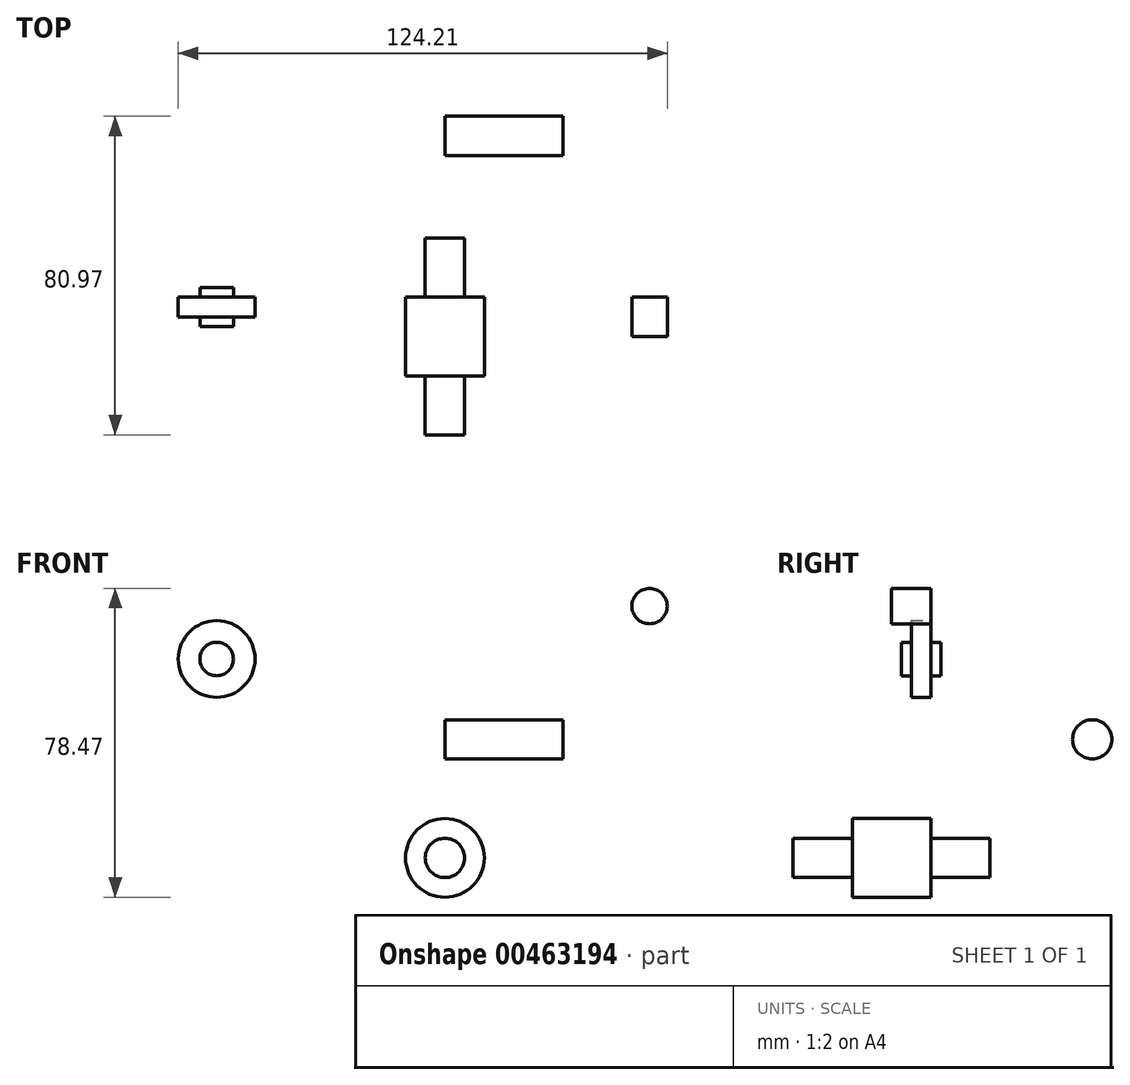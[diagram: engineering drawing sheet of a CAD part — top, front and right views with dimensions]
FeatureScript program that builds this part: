
annotation { "Feature Type Name" : "Feature", "Feature Type Description" : "" }
export const myFeature = defineFeature(function(context is Context, id is Id, definition is map)
    precondition{}
    {
        {
            var Q0;
            Q0=qCreatedBy(makeId("Front.planeOp"),FACE);
            var sketch = newSketch(context, id + "F0", { "sketchPlane" : qUnion([Q0])});
            skCircle(sketch, "E0", {"center": v(0, 0) * mm, "radius": 10 * mm});
            skCircle(sketch, "E1", {"center": v(0, 0) * mm, "radius": 4.99 * mm});
            skCircle(sketch, "E2", {"center": v(-57.98, 50.53) * mm, "radius": 9.75 * mm});
            skCircle(sketch, "E3", {"center": v(-57.98, 50.53) * mm, "radius": 4.25 * mm});
            skCircle(sketch, "E4", {"center": v(52, 63.98) * mm, "radius": 4.49 * mm});
            skSolve(sketch);
        }
        {
            var Q0;
            Q0=makeQuery(id+"F0.imprint","IMPRINT",FACE,{"disambiguationData":[TD([[makeQuery(id+"F0.imprint","IMPRINT",EDGE,{"derivedFrom":sQuery(id+"F0.wireOp",EDGE,"E0")}),1.0]])]});
            var Q1;
            Q1=makeQuery(id+"F0.imprint","IMPRINT",FACE,{"disambiguationData":[TD([[makeQuery(id+"F0.imprint","IMPRINT",EDGE,{"derivedFrom":sQuery(id+"F0.wireOp",EDGE,"E1")}),1.0]])]});
            extrude(context, id + "F1", {"entities" : qUnion([Q0, Q1]), "depth" : 20 * mm});
        }
        {
            var Q0;
            Q0=makeQuery(id+"F0.imprint","IMPRINT",FACE,{"disambiguationData":[TD([[makeQuery(id+"F0.imprint","IMPRINT",EDGE,{"derivedFrom":sQuery(id+"F0.wireOp",EDGE,"E1")}),1.0]])]});
            extrude(context, id + "F2", {"entities" : qUnion([Q0]), "operationType" : NewBodyOperationType.ADD, "oppositeDirection" : true, "depth" : 15 * mm});
        }
        {
            var Q0;
            Q0=makeQuery(id+"F1.opExtrude","CAP_FACE",FACE,{"disambiguationData":[OSD([sQuery(id+"F0.wireOp",EDGE,"E0")])],"isStart":false});
            var sketch = newSketch(context, id + "F3", { "sketchPlane" : qUnion([Q0])});
            skCircle(sketch, "E5.0", {"center": v(0, 0) * mm, "radius": 4.99 * mm});
            skSolve(sketch);
        }
        {
            var Q0;
            Q0=makeQuery(id+"F3.imprint","IMPRINT",FACE,{"disambiguationData":[TD([[makeQuery(id+"F3.imprint","IMPRINT",EDGE,{"derivedFrom":sQuery(id+"F3.wireOp",EDGE,"E5.0")}),1.0]])]});
            extrude(context, id + "F4", {"entities" : qUnion([Q0]), "operationType" : NewBodyOperationType.ADD, "depth" : 15 * mm});
        }
        {
            var Q0;
            Q0=makeQuery(id+"F0.imprint","IMPRINT",FACE,{"disambiguationData":[TD([[makeQuery(id+"F0.imprint","IMPRINT",EDGE,{"derivedFrom":sQuery(id+"F0.wireOp",EDGE,"E4")}),1.0]])]});
            extrude(context, id + "F5", {"entities" : qUnion([Q0]), "depth" : 10 * mm});
        }
        {
            var Q0;
            Q0=makeQuery(id+"F0.imprint","IMPRINT",FACE,{"disambiguationData":[TD([[makeQuery(id+"F0.imprint","IMPRINT",EDGE,{"derivedFrom":sQuery(id+"F0.wireOp",EDGE,"E2")}),1.0]])]});
            var Q1;
            Q1=makeQuery(id+"F0.imprint","IMPRINT",FACE,{"disambiguationData":[TD([[makeQuery(id+"F0.imprint","IMPRINT",EDGE,{"derivedFrom":sQuery(id+"F0.wireOp",EDGE,"E3")}),1.0]])]});
            extrude(context, id + "F6", {"entities" : qUnion([Q0, Q1]), "depth" : 5 * mm});
        }
        {
            var Q0;
            Q0=makeQuery(id+"F0.imprint","IMPRINT",FACE,{"disambiguationData":[TD([[makeQuery(id+"F0.imprint","IMPRINT",EDGE,{"derivedFrom":sQuery(id+"F0.wireOp",EDGE,"E3")}),1.0]])]});
            extrude(context, id + "F7", {"entities" : qUnion([Q0]), "operationType" : NewBodyOperationType.ADD, "oppositeDirection" : true, "depth" : 2.5 * mm});
        }
        {
            var Q0;
            Q0=makeQuery(id+"F6.opExtrude","CAP_FACE",FACE,{"disambiguationData":[OSD([sQuery(id+"F0.wireOp",EDGE,"E2")])],"isStart":false});
            var sketch = newSketch(context, id + "F8", { "sketchPlane" : qUnion([Q0])});
            skCircle(sketch, "E6.0", {"center": v(-57.98, 50.53) * mm, "radius": 4.25 * mm});
            skSolve(sketch);
        }
        {
            var Q0;
            Q0=makeQuery(id+"F8.imprint","IMPRINT",FACE,{"disambiguationData":[TD([[makeQuery(id+"F8.imprint","IMPRINT",EDGE,{"derivedFrom":sQuery(id+"F8.wireOp",EDGE,"E6.0")}),1.0]])]});
            extrude(context, id + "F9", {"entities" : qUnion([Q0]), "operationType" : NewBodyOperationType.ADD, "depth" : 2.5 * mm});
        }
        {
            var Q0;
            Q0=qCreatedBy(makeId("Right.planeOp"),FACE);
            var sketch = newSketch(context, id + "F10", { "sketchPlane" : qUnion([Q0])});
            skCircle(sketch, "E7", {"center": v(40.98, 30.13) * mm, "radius": 4.99 * mm});
            skSolve(sketch);
        }
        {
            var Q0;
            Q0=makeQuery(id+"F10.imprint","IMPRINT",FACE,{"disambiguationData":[TD([[makeQuery(id+"F10.imprint","IMPRINT",EDGE,{"derivedFrom":sQuery(id+"F10.wireOp",EDGE,"E7")}),1.0]])]});
            extrude(context, id + "F11", {"entities" : qUnion([Q0]), "depth" : 30 * mm});
        }
    });
